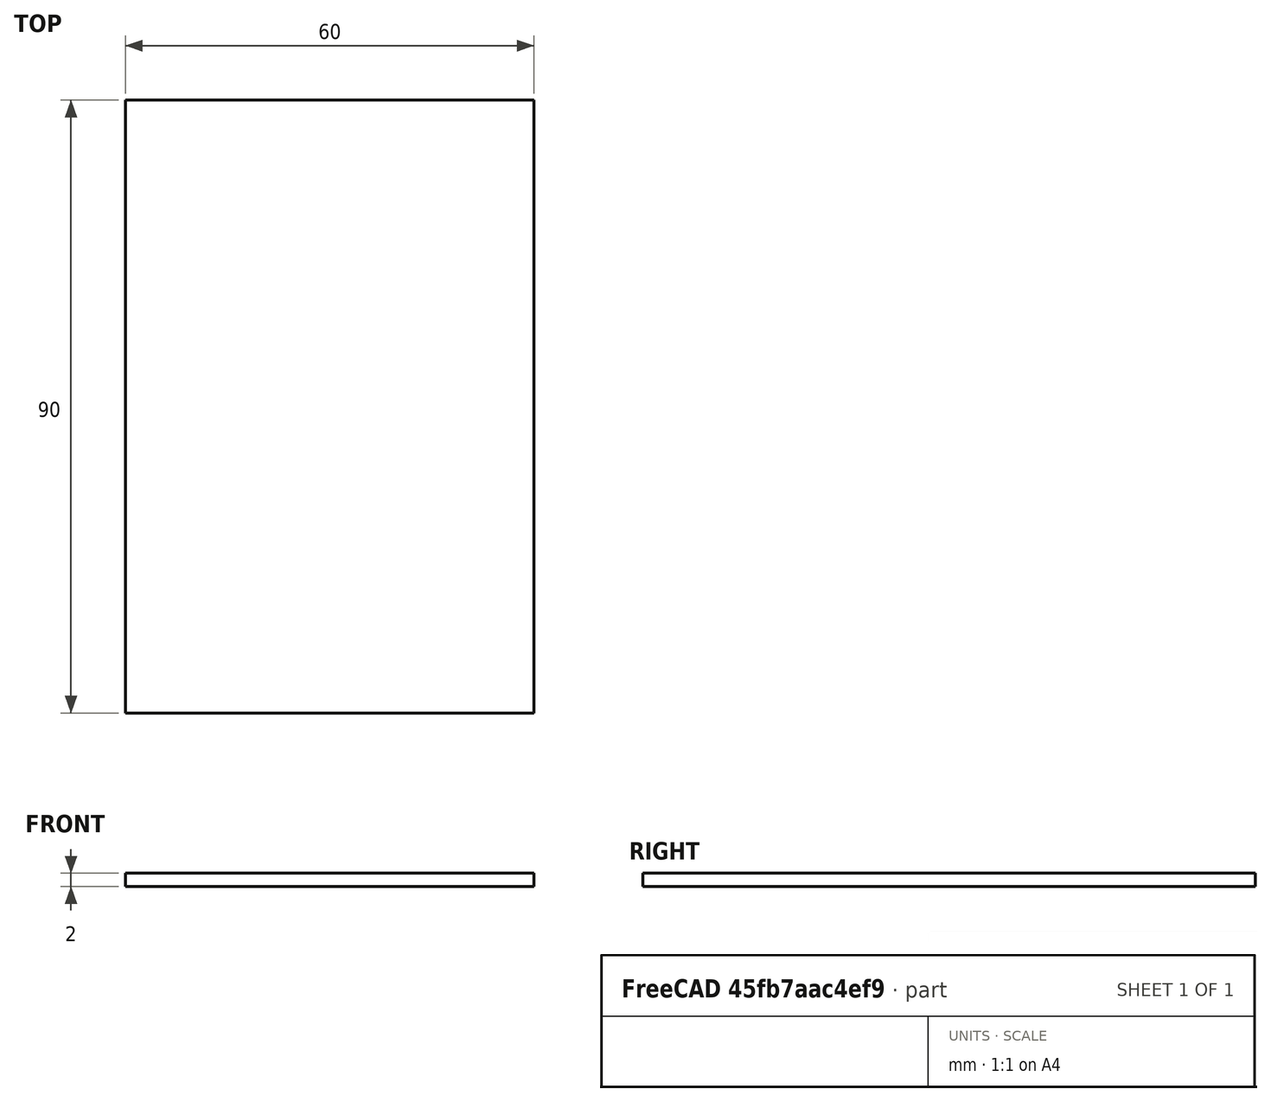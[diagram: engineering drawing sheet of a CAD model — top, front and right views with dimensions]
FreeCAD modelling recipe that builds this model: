
FCSTD DOCUMENT  (FreeCAD 0.20R29177 (Git))
Label: cabine_part3
License: All rights reserved
LicenseURL: http://en.wikipedia.org/wiki/All_rights_reserved
objects: Sketcher::SketchObject×1, PartDesign::Pad×1, PartDesign::Body×1
note: 4 computed .brp shape members not serialized (recipe doc carries the construction recipe); baked Part::Feature solids carry a one-line shape summary decoded from their .brp

FEATURE [Sketcher::SketchObject] Sketch003
  FullyConstrained = true
  MapMode = 5
  Placement = pos=(0,1.2e-14,54) rot=(0,0,1;3.14159rad)
  sketch-geometry (4):
    g0: LineSegment StartX=-120 StartY=9 StartZ=0 EndX=-60 EndY=9 EndZ=0
    g1: LineSegment StartX=-60 StartY=9 StartZ=0 EndX=-60 EndY=-81 EndZ=0
    g2: LineSegment StartX=-60 StartY=-81 StartZ=0 EndX=-120 EndY=-81 EndZ=0
    g3: LineSegment StartX=-120 StartY=-81 StartZ=0 EndX=-120 EndY=9 EndZ=0
  constraints (12):
    c: Coincident(g0,g1)
    c: Coincident(g1,g2)
    c: Coincident(g2,g3)
    c: Coincident(g3,g0)
    c: Horizontal(g0)
    c: Horizontal(g2)
    c: Vertical(g1)
    c: Vertical(g3)
    c: DistanceY(g1,g1) = 90
    c: DistanceX(g0,g0) = 60
    c: DistanceY(g-1,g0) = 9
    c: DistanceX(g0,g-1) = 60
FEATURE [PartDesign::Pad] Pad003
  Direction = (0,2e-16,1)
  Length = 2
  Length2 = 10
  Placement = pos=(0,1.2e-14,54) rot=(0,0,1;3.14159rad)
  Profile = -> Sketch003
  ReferenceAxis = -> Sketch003 [N_Axis]
  Reversed = true
  Type = 0
FEATURE [PartDesign::Body] Body
  Group = -> [Sketch003,Pad003]
  Origin = -> Origin
  Tip = -> Pad003
